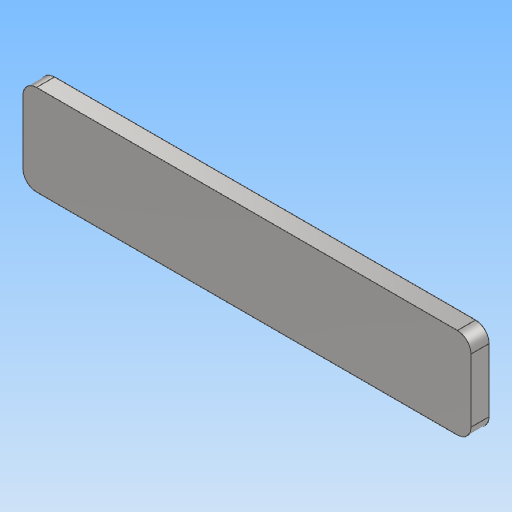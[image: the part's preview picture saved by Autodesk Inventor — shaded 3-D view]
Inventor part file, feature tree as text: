
AUTODESK INVENTOR PART (.ipt)
format: ipt  version: 2020 (Build 240168000, 168)  size: 120,320 bytes
history: native  units: mm
features: other x1, extrude x1
ambient origin geometry x8: Origin, YZ Plane, XZ Plane, XY Plane, X Axis, Y Axis, Z Axis, Center Point
bodies: Body1 (feature_tree)
feature tree (2):
  other  "實體1"
  extrude  "擠出1"  Depth=49.5mm
